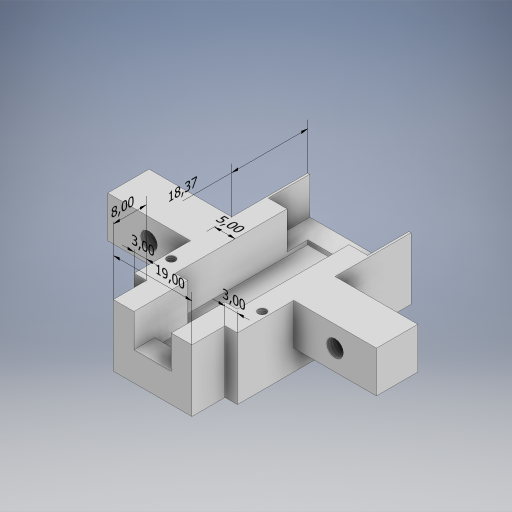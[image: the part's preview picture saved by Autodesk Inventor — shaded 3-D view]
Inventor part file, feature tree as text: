
AUTODESK INVENTOR PART (.ipt)
format: ipt  version: 2023 (Build 270158000, 158)  size: 398,848 bytes
history: native  units: mm
features: other x7, sketch x7, extrude x6, thread x4
ambient origin geometry x8: Origin, YZ Plane, XZ Plane, XY Plane, X Axis, Y Axis, Z Axis, Center Point
bodies: Solid1 (feature_tree)
feature tree (24):
  other  "Annotations"
  extrude  "Extrusion1"  Depth=32.0mm
  extrude  "Extrusion3"  Depth=3.0mm
  extrude  "Extrusion4"  Depth=8.0mm
  extrude  "Extrusion5"  Depth=5.0mm
  extrude  "Extrusion6"  Depth=5.0mm
  thread  "Thread1"  [1 undecoded]
  thread  "Thread2"  [1 undecoded]
  sketch  "Sketch7"  dims[d12=5.0mm d13=5.0mm d14=10.0mm d15=0.0mm d24=0.5mm]
  extrude  "Extrusion7"  Depth=5.0mm
  thread  "Thread3"  [1 undecoded]
  thread  "Thread4"  [1 undecoded]
  sketch  "Sketch1"  dims[d0=15.0mm d1=32.0mm]
  sketch  "Sketch3"  dims[d2=9.0mm d3=3.0mm]
  sketch  "Sketch4"  dims[d4=3.0mm d5=8.0mm]
  sketch  "Sketch5"  dims[d6=5.0mm d7=5.0mm]
  sketch  "Sketch6"  dims[d8=5.0mm d9=5.0mm d10=5.0mm d11=5.0mm]
  sketch  "Sketch8"  dims[d25=0.5mm d26=1.0mm d27=0.0mm d28=10.0mm d29=0.0mm d30=2.0mm d31=0.0mm d32=5.0mm d33=5.0mm d34=10.0mm d35=0.0mm d36=5.0mm d37=0.0mm d59=2.0mm d60=7.5mm d61=1.5mm d62=2.0mm d63=7.5mm d64=1.5mm d65=5.0mm d66=0.0mm d67=5.0mm d68=0.0mm d69=5.0mm d70=0.0mm d71=20.0mm d72=10.0mm d73=20.0mm d74=10.0mm d76=4.0mm d77=4.0mm d78=10.0mm d79=10.0mm d80=5.0mm d81=5.0mm d82=10.0mm d83=0.0mm d84=10.0mm d85=0.0mm d86=10.0mm d87=0.0mm d41=0.0mm d42=10.0mm d43=18.365958mm d44=0.0mm d45=10.0mm d46=8.0mm d47=0.0mm d48=10.0mm d49=3.0mm d50=0.0mm d51=10.0mm d52=3.0mm d53=8.245235mm d54=9.173282mm d55=19.0mm d56=3.631466mm d57=6.698263mm d58=5.0mm]
  other  "Linear Dimension 1"
  other  "Linear Dimension 2"
  other  "Linear Dimension 3"
  other  "Linear Dimension 4"
  other  "Linear Dimension 5"
  other  "Linear Dimension 6"
note: 4 required parameter values undecoded (feature->parameter linkage not recoverable at this tier; creation-order binding heuristic only, values carry confidence <= 0.55)
